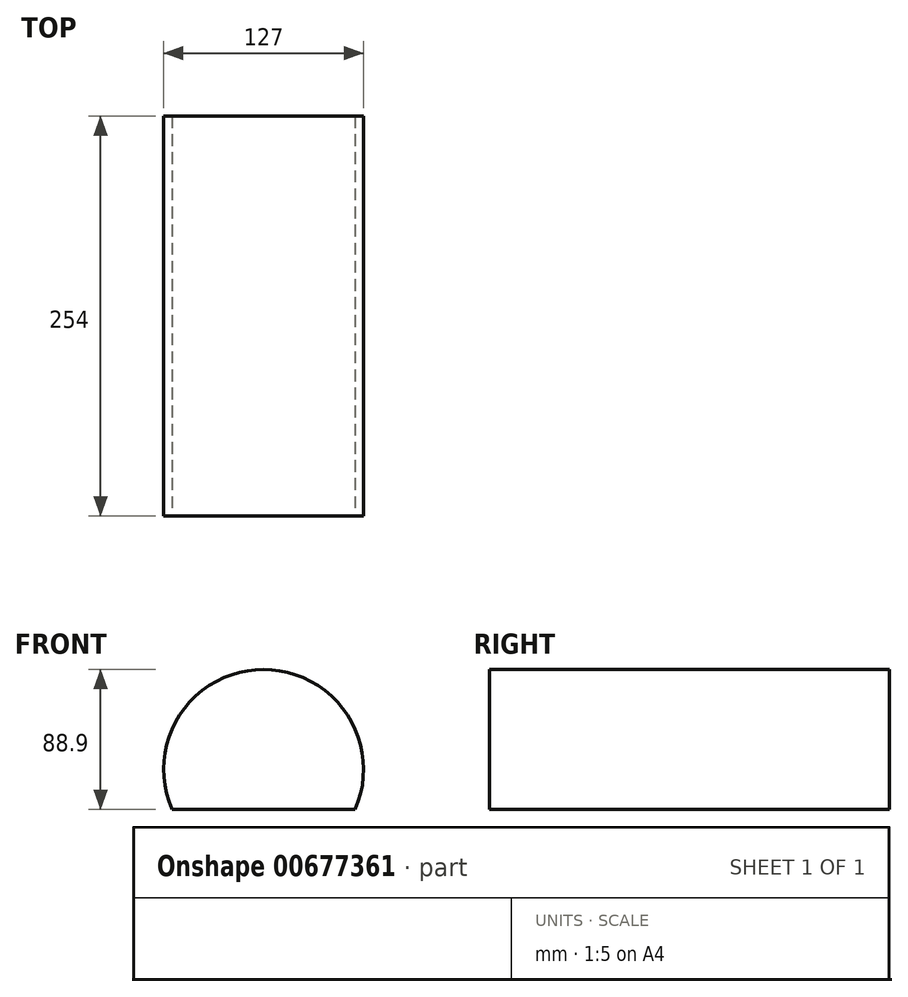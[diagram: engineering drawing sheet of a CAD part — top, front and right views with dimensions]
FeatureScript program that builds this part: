
annotation { "Feature Type Name" : "Feature", "Feature Type Description" : "" }
export const myFeature = defineFeature(function(context is Context, id is Id, definition is map)
    precondition{}
    {
        {
            var Q0;
            Q0=qCreatedBy(makeId("Front.planeOp"),FACE);
            var sketch = newSketch(context, id + "F0", { "sketchPlane" : qUnion([Q0])});
            skArc(sketch, "E0", {"start": v(58.2, -25.4) * mm, "mid": v(0, 63.5) * mm, "end": v(-58.2, -25.4) * mm});
            skLineSegment(sketch, "E1", {"start": v(-58.2, -25.4) * mm, "end": v(58.2, -25.4) * mm});
            skLineSegment(sketch, "E2", {"start": v(0, 0) * mm, "end": v(0, -25.4) * mm});
            skSolve(sketch);
        }
        {
            var Q0;
            {var subQ0=sQuery(id+"F0.wireOp",EDGE,"E0");Q0=makeQuery(id+"F0.imprint","IMPRINT",FACE,{"disambiguationData":[TD([[makeQuery(id+"F0.imprint","IMPRINT",EDGE,{"derivedFrom":subQ0}),1.0]])]});}
            extrude(context, id + "F1", {"entities" : qUnion([Q0]), "depth" : -254 * mm, "offsetDistance" : 25.4 * mm});
        }
    });
